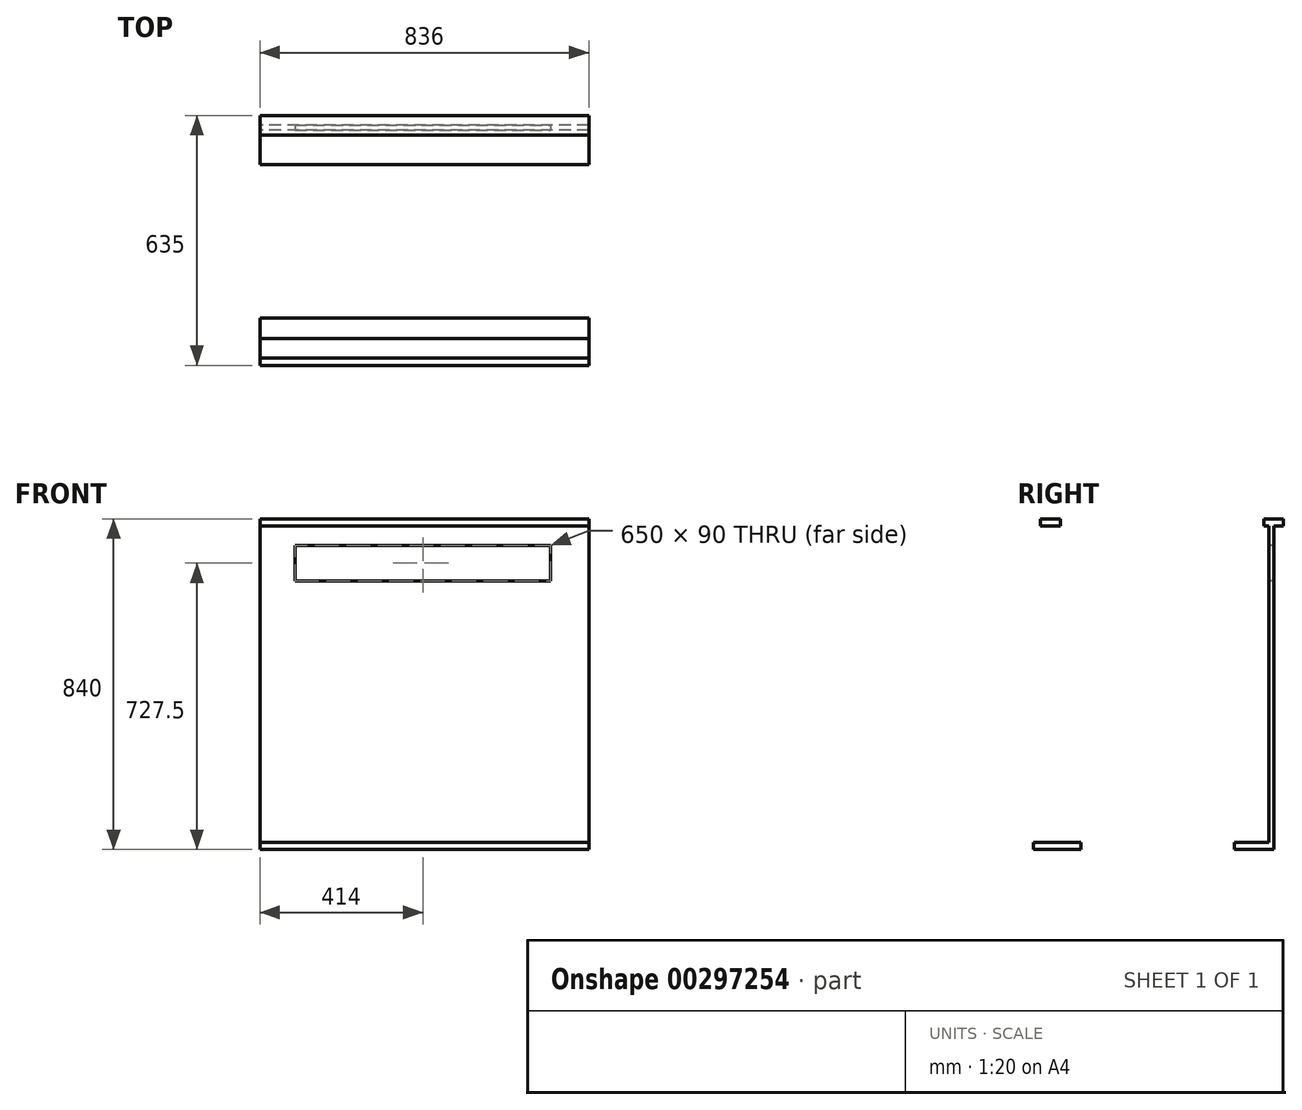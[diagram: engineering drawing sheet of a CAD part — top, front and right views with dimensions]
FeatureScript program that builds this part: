
annotation { "Feature Type Name" : "Feature", "Feature Type Description" : "" }
export const myFeature = defineFeature(function(context is Context, id is Id, definition is map)
    precondition{}
    {
        {
            var Q0;
            Q0=qCreatedBy(makeId("Right.planeOp"),FACE);
            var sketch = newSketch(context, id + "F0", { "sketchPlane" : qUnion([Q0])});
            skLineSegment(sketch, "E0.bottom", {"start": v(317.5, 420) * mm, "end": v(-317.5, 420) * mm, "construction": true});
            skLineSegment(sketch, "E0.right", {"start": v(-317.5, 420) * mm, "end": v(-317.5, -420) * mm, "construction": true});
            skPoint(sketch, "E0.middle", {"position": v(0, 0) * mm});
            skLineSegment(sketch, "E1.bottom", {"start": v(-299.5, 420) * mm, "end": v(-249.5, 420) * mm});
            skLineSegment(sketch, "E1.top", {"start": v(-299.5, 402) * mm, "end": v(-249.5, 402) * mm});
            skLineSegment(sketch, "E1.left", {"start": v(-299.5, 420) * mm, "end": v(-299.5, 402) * mm});
            skLineSegment(sketch, "E1.right", {"start": v(-249.5, 420) * mm, "end": v(-249.5, 402) * mm});
            skLineSegment(sketch, "E2.bottom", {"start": v(-317.5, -420) * mm, "end": v(-197.5, -420) * mm});
            skLineSegment(sketch, "E2.top", {"start": v(-317.5, -402) * mm, "end": v(-197.5, -402) * mm});
            skLineSegment(sketch, "E2.left", {"start": v(-317.5, -420) * mm, "end": v(-317.5, -402) * mm});
            skLineSegment(sketch, "E2.right", {"start": v(-197.5, -420) * mm, "end": v(-197.5, -402) * mm});
            skLineSegment(sketch, "E3.bottom", {"start": v(280.5, -402) * mm, "end": v(292.5, -402) * mm});
            skLineSegment(sketch, "E3.top", {"start": v(280.5, 402) * mm, "end": v(292.5, 402) * mm});
            skLineSegment(sketch, "E3.left", {"start": v(280.5, -402) * mm, "end": v(280.5, 402) * mm});
            skLineSegment(sketch, "E3.right", {"start": v(292.5, -402) * mm, "end": v(292.5, 402) * mm});
            skLineSegment(sketch, "E4.bottom", {"start": v(317.5, 420) * mm, "end": v(267.5, 420) * mm});
            skLineSegment(sketch, "E4.top", {"start": v(317.5, 402) * mm, "end": v(267.5, 402) * mm});
            skLineSegment(sketch, "E4.left", {"start": v(317.5, 420) * mm, "end": v(317.5, 402) * mm});
            skLineSegment(sketch, "E4.right", {"start": v(267.5, 420) * mm, "end": v(267.5, 402) * mm});
            skLineSegment(sketch, "E5", {"start": v(317.5, 420) * mm, "end": v(317.5, -420) * mm, "construction": true});
            skLineSegment(sketch, "E6.bottom", {"start": v(292.5, -402) * mm, "end": v(192.5, -402) * mm});
            skLineSegment(sketch, "E6.top", {"start": v(292.5, -420) * mm, "end": v(192.5, -420) * mm});
            skLineSegment(sketch, "E6.left", {"start": v(292.5, -402) * mm, "end": v(292.5, -420) * mm});
            skLineSegment(sketch, "E6.right", {"start": v(192.5, -402) * mm, "end": v(192.5, -420) * mm});
            skLineSegment(sketch, "E7", {"start": v(-197.5, -420) * mm, "end": v(192.5, -420) * mm, "construction": true});
            skSolve(sketch);
        }
        {
            var Q0;
            Q0=qSketchRegion(id+"F0",true);
            extrude(context, id + "F1", {"entities" : qUnion([Q0]), "depth" : 836 * mm});
        }
        {
            var Q0;
            Q0=makeQuery(id+"F1.opExtrude","SWEPT_FACE",FACE,{"disambiguationData":[OSD([sQuery(id+"F0.wireOp",EDGE,"E3.left")])]});
            var sketch = newSketch(context, id + "F2", { "sketchPlane" : qUnion([Q0])});
            skLineSegment(sketch, "E8.bottom", {"start": v(89, 262.5) * mm, "end": v(739, 262.5) * mm});
            skLineSegment(sketch, "E8.top", {"start": v(89, 352.5) * mm, "end": v(739, 352.5) * mm});
            skLineSegment(sketch, "E8.left", {"start": v(89, 262.5) * mm, "end": v(89, 352.5) * mm});
            skLineSegment(sketch, "E8.right", {"start": v(739, 262.5) * mm, "end": v(739, 352.5) * mm});
            skLineSegment(sketch, "E9", {"start": v(89, 307.5) * mm, "end": v(739, 307.5) * mm, "construction": true});
            skSolve(sketch);
        }
        {
            var Q0;
            Q0=makeQuery(id+"F2.imprint","IMPRINT",FACE,{"disambiguationData":[TD([[makeQuery(id+"F2.imprint","IMPRINT",EDGE,{"derivedFrom":sQuery(id+"F2.wireOp",EDGE,"E8.bottom")}),1.0]])]});
            extrude(context, id + "F3", {"entities" : qUnion([Q0]), "operationType" : NewBodyOperationType.REMOVE, "oppositeDirection" : true, "depth" : 12 * mm});
        }
    });
